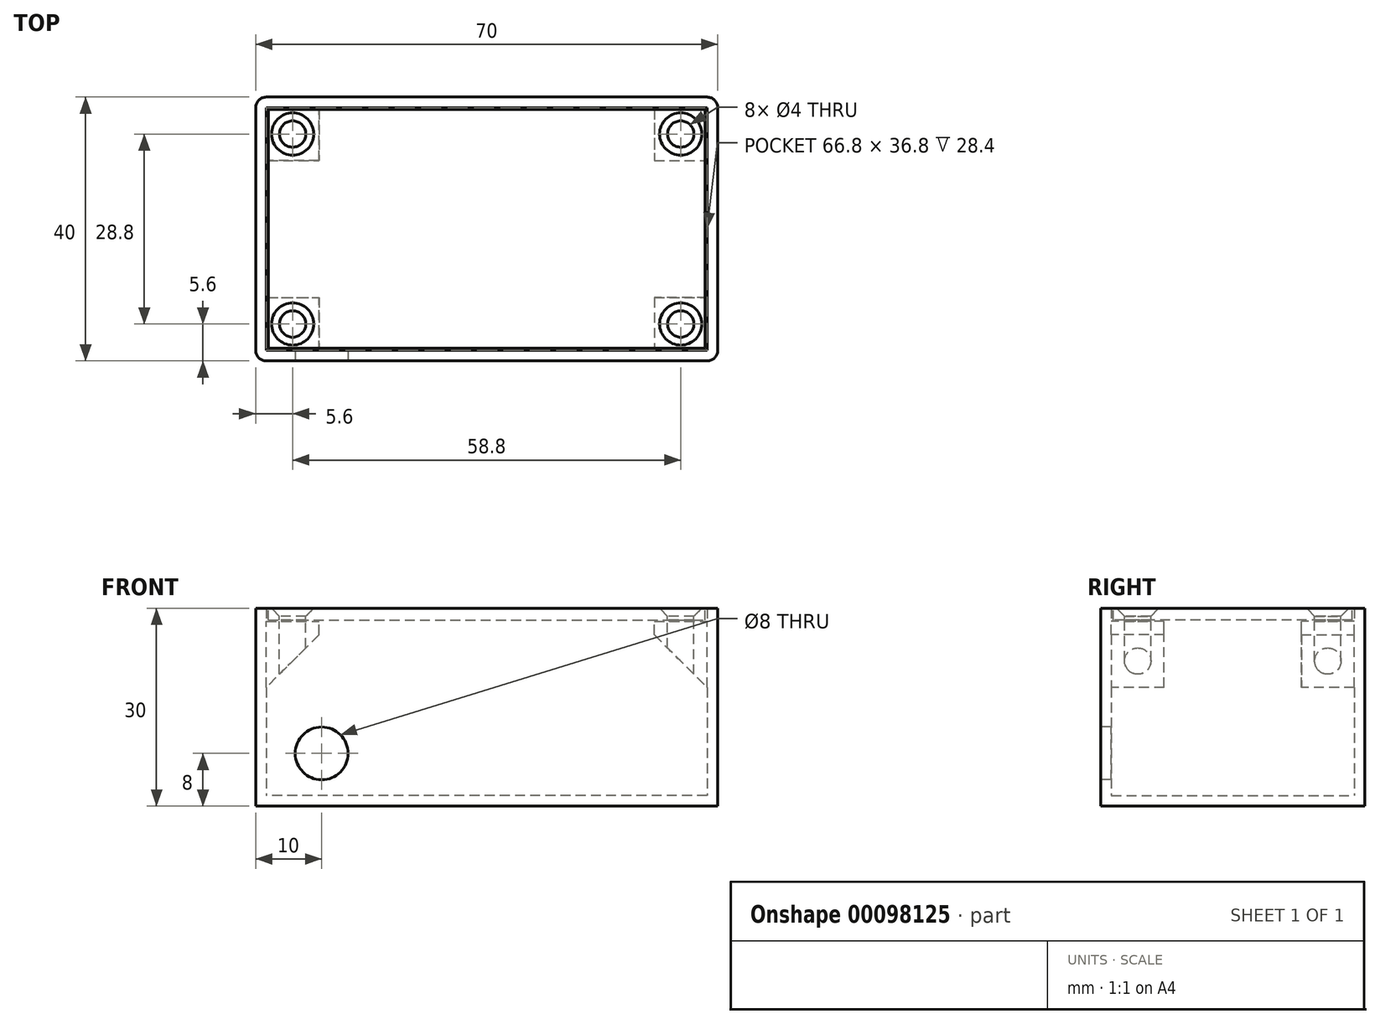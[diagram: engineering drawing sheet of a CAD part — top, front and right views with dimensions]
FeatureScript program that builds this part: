
annotation { "Feature Type Name" : "Feature", "Feature Type Description" : "" }
export const myFeature = defineFeature(function(context is Context, id is Id, definition is map)
    precondition{}
    {
        {
            var Q0;
            Q0=qCreatedBy(makeId("Top.planeOp"),FACE);
            var sketch = newSketch(context, id + "F0", { "sketchPlane" : qUnion([Q0])});
            skLineSegment(sketch, "E0.bottom", {"start": v(0, 0) * mm, "end": v(-70, 0) * mm});
            skLineSegment(sketch, "E0.top", {"start": v(0, 40) * mm, "end": v(-70, 40) * mm});
            skLineSegment(sketch, "E0.left", {"start": v(0, 0) * mm, "end": v(0, 40) * mm});
            skLineSegment(sketch, "E0.right", {"start": v(-70, 0) * mm, "end": v(-70, 40) * mm});
            skSolve(sketch);
        }
        {
            var Q0;
            Q0=makeQuery(id+"F0.imprint","IMPRINT",FACE,{"disambiguationData":[TD([[makeQuery(id+"F0.imprint","IMPRINT",EDGE,{"derivedFrom":sQuery(id+"F0.wireOp",EDGE,"E0.bottom")}),-1.0]])]});
            extrude(context, id + "F1", {"entities" : qUnion([Q0]), "depth" : 30 * mm});
        }
        {
            var Q0;
            Q0=makeQuery(id+"F1.opExtrude","CAP_FACE",FACE,{"disambiguationData":[OSD([sQuery(id+"F0.wireOp",EDGE,"E0.bottom"),sQuery(id+"F0.wireOp",EDGE,"E0.top"),sQuery(id+"F0.wireOp",EDGE,"E0.left"),sQuery(id+"F0.wireOp",EDGE,"E0.right")])],"isStart":false});
            shell(context, id + "F2", {"entities" : qUnion([Q0]), "thickness" : 1.6 * mm});
        }
        {
            var Q0;
            Q0=makeQuery(id+"F1.opExtrude","CAP_FACE",FACE,{"disambiguationData":[OSD([sQuery(id+"F0.wireOp",EDGE,"E0.bottom"),sQuery(id+"F0.wireOp",EDGE,"E0.top"),sQuery(id+"F0.wireOp",EDGE,"E0.left"),sQuery(id+"F0.wireOp",EDGE,"E0.right")])],"isStart":false});
            var Q1;
            Q1 = qBodyType(qCreatedBy(id + "F4" ,EDGE), BodyType.WIRE);
            cPlane(context, id + "F3", {"entities" : qUnion([Q0, Q1]), "cplaneType" : CPlaneType.OFFSET, "offset" : 2 * mm, "oppositeDirection" : true, "width" : 150 * mm, "height" : 150 * mm});
        }
        {
            var Q0;
            Q0=qCreatedBy(id+"F3.planeOp",FACE);
            var sketch = newSketch(context, id + "F4", { "sketchPlane" : qUnion([Q0])});
            skLineSegment(sketch, "E1.bottom", {"start": v(-68.4, 38.4) * mm, "end": v(-60.4, 38.4) * mm});
            skLineSegment(sketch, "E1.top", {"start": v(-68.4, 30.4) * mm, "end": v(-60.4, 30.4) * mm});
            skLineSegment(sketch, "E1.left", {"start": v(-68.4, 38.4) * mm, "end": v(-68.4, 30.4) * mm});
            skLineSegment(sketch, "E1.right", {"start": v(-60.4, 38.4) * mm, "end": v(-60.4, 30.4) * mm});
            skLineSegment(sketch, "E2.bottom", {"start": v(-9.6, 38.4) * mm, "end": v(-1.6, 38.4) * mm});
            skLineSegment(sketch, "E2.top", {"start": v(-9.6, 30.4) * mm, "end": v(-1.6, 30.4) * mm});
            skLineSegment(sketch, "E2.left", {"start": v(-9.6, 38.4) * mm, "end": v(-9.6, 30.4) * mm});
            skLineSegment(sketch, "E2.right", {"start": v(-1.6, 38.4) * mm, "end": v(-1.6, 30.4) * mm});
            skLineSegment(sketch, "E3.bottom", {"start": v(-9.6, 9.6) * mm, "end": v(-1.6, 9.6) * mm});
            skLineSegment(sketch, "E3.top", {"start": v(-9.6, 1.6) * mm, "end": v(-1.6, 1.6) * mm});
            skLineSegment(sketch, "E3.left", {"start": v(-9.6, 9.6) * mm, "end": v(-9.6, 1.6) * mm});
            skLineSegment(sketch, "E3.right", {"start": v(-1.6, 9.6) * mm, "end": v(-1.6, 1.6) * mm});
            skLineSegment(sketch, "E4.bottom", {"start": v(-68.4, 9.6) * mm, "end": v(-60.4, 9.6) * mm});
            skLineSegment(sketch, "E4.top", {"start": v(-68.4, 1.6) * mm, "end": v(-60.4, 1.6) * mm});
            skLineSegment(sketch, "E4.left", {"start": v(-68.4, 9.6) * mm, "end": v(-68.4, 1.6) * mm});
            skLineSegment(sketch, "E4.right", {"start": v(-60.4, 9.6) * mm, "end": v(-60.4, 1.6) * mm});
            skCircle(sketch, "E5", {"center": v(-64.4, 34.4) * mm, "radius": 2 * mm});
            skPoint(sketch, "E5.centerSnap0", {"position": v(-64.4, 38.4) * mm});
            skPoint(sketch, "E5.centerSnap1", {"position": v(-60.4, 34.4) * mm});
            skCircle(sketch, "E6", {"center": v(-5.6, 34.4) * mm, "radius": 2 * mm});
            skPoint(sketch, "E6.centerSnap0", {"position": v(-9.6, 34.4) * mm});
            skPoint(sketch, "E6.centerSnap1", {"position": v(-5.6, 38.4) * mm});
            skCircle(sketch, "E7", {"center": v(-64.4, 5.6) * mm, "radius": 2 * mm});
            skPoint(sketch, "E7.centerSnap0", {"position": v(-60.4, 5.6) * mm});
            skPoint(sketch, "E7.centerSnap1", {"position": v(-64.4, 9.6) * mm});
            skCircle(sketch, "E8", {"center": v(-5.6, 5.6) * mm, "radius": 2 * mm});
            skPoint(sketch, "E8.centerSnap0", {"position": v(-9.6, 5.6) * mm});
            skPoint(sketch, "E8.centerSnap1", {"position": v(-5.6, 9.6) * mm});
            skSolve(sketch);
        }
        {
            var Q0;
            Q0 = qSketchRegion(id + "F4", true);
            extrude(context, id + "F5", {"entities" : qUnion([Q0]), "operationType" : NewBodyOperationType.ADD, "oppositeDirection" : true, "depth" : 10 * mm});
        }
        {
            var Q0;
            Q0=makeQuery(id+"F5.opExtrude","CAP_EDGE",EDGE,{"disambiguationData":[OSD([sQuery(id+"F4.wireOp",EDGE,"E1.right")])],"isStart":false});
            var Q1;
            Q1=makeQuery(id+"F5.opExtrude","CAP_EDGE",EDGE,{"disambiguationData":[OSD([sQuery(id+"F4.wireOp",EDGE,"E2.left")])],"isStart":false});
            var Q2;
            Q2=makeQuery(id+"F5.opExtrude","CAP_EDGE",EDGE,{"disambiguationData":[OSD([sQuery(id+"F4.wireOp",EDGE,"E4.right")])],"isStart":false});
            var Q3;
            Q3=makeQuery(id+"F5.opExtrude","CAP_EDGE",EDGE,{"disambiguationData":[OSD([sQuery(id+"F4.wireOp",EDGE,"E3.left")])],"isStart":false});
            chamfer(context, id + "F6", {"entities" : qUnion([Q0, Q1, Q2, Q3]), "width" : 8 * mm, "tangentPropagation" : true});
        }
        {
            var Q0;
            Q0=makeQuery(id+"F1.opExtrude","SWEPT_FACE",FACE,{"disambiguationData":[OSD([sQuery(id+"F0.wireOp",EDGE,"E0.bottom")])]});
            var sketch = newSketch(context, id + "F7", { "sketchPlane" : qUnion([Q0])});
            skCircle(sketch, "E9", {"center": v(-60, 8) * mm, "radius": 4 * mm});
            skSolve(sketch);
        }
        {
            var Q0;
            Q0 = qSketchRegion(id + "F7", true);
            var Q1;
            Q1=makeQuery(id+"F2.opShell","OFFSET_FACE",FACE,{"disambiguationData":[OSD([sQuery(id+"F0.wireOp",EDGE,"E0.bottom")])]});
            extrude(context, id + "F8", {"entities" : qUnion([Q0]), "operationType" : NewBodyOperationType.REMOVE, "endBound" : BoundingType.UP_TO_SURFACE, "oppositeDirection" : true, "endBoundEntityFace" : qUnion([Q1]), "depth" : 25 * mm});
        }
        {
            var Q0;
            Q0=makeQuery(id+"F1.opExtrude","CAP_FACE",FACE,{"disambiguationData":[OSD([sQuery(id+"F0.wireOp",EDGE,"E0.bottom"),sQuery(id+"F0.wireOp",EDGE,"E0.top"),sQuery(id+"F0.wireOp",EDGE,"E0.left"),sQuery(id+"F0.wireOp",EDGE,"E0.right")])],"isStart":false});
            var sketch = newSketch(context, id + "F9", { "sketchPlane" : qUnion([Q0])});
            skLineSegment(sketch, "E10.bottom", {"start": v(-68.1, 38.1) * mm, "end": v(-1.9, 38.1) * mm});
            skLineSegment(sketch, "E10.top", {"start": v(-68.1, 1.9) * mm, "end": v(-1.9, 1.9) * mm});
            skLineSegment(sketch, "E10.left", {"start": v(-68.1, 38.1) * mm, "end": v(-68.1, 1.9) * mm});
            skLineSegment(sketch, "E10.right", {"start": v(-1.9, 38.1) * mm, "end": v(-1.9, 1.9) * mm});
            skCircle(sketch, "E11", {"center": v(-64.4, 34.4) * mm, "radius": 2 * mm});
            skCircle(sketch, "E12", {"center": v(-5.6, 34.4) * mm, "radius": 2 * mm});
            skCircle(sketch, "E13", {"center": v(-64.4, 5.6) * mm, "radius": 2 * mm});
            skCircle(sketch, "E14", {"center": v(-5.6, 5.6) * mm, "radius": 2 * mm});
            skSolve(sketch);
        }
        {
            var Q0;
            Q0 = qSketchRegion(id + "F9", true);
            extrude(context, id + "F10", {"entities" : qUnion([Q0]), "oppositeDirection" : true, "depth" : 1.8 * mm});
        }
        {
            var Q0;
            Q0=makeQuery(id+"F10.opExtrude","CAP_EDGE",EDGE,{"disambiguationData":[OSD([sQuery(id+"F9.wireOp",EDGE,"E11")])],"isStart":true});
            var Q1;
            Q1=makeQuery(id+"F10.opExtrude","CAP_EDGE",EDGE,{"disambiguationData":[OSD([sQuery(id+"F9.wireOp",EDGE,"E12")])],"isStart":true});
            var Q2;
            Q2=makeQuery(id+"F10.opExtrude","CAP_EDGE",EDGE,{"disambiguationData":[OSD([sQuery(id+"F9.wireOp",EDGE,"E14")])],"isStart":true});
            var Q3;
            Q3=makeQuery(id+"F10.opExtrude","CAP_EDGE",EDGE,{"disambiguationData":[OSD([sQuery(id+"F9.wireOp",EDGE,"E13")])],"isStart":true});
            chamfer(context, id + "F11", {"entities" : qUnion([Q0, Q1, Q2, Q3]), "width" : 1.2 * mm, "tangentPropagation" : true});
        }
        {
            var Q0;
            Q0=makeQuery(id+"F1.opExtrude","SWEPT_EDGE",EDGE,{"disambiguationData":[OSD([sQuery(id+"F0.wireOp",EDGE,"E0.bottom"),sQuery(id+"F0.wireOp",EDGE,"E0.right")])]});
            var Q1;
            Q1=makeQuery(id+"F1.opExtrude","SWEPT_EDGE",EDGE,{"disambiguationData":[OSD([sQuery(id+"F0.wireOp",EDGE,"E0.bottom"),sQuery(id+"F0.wireOp",EDGE,"E0.left")])]});
            var Q2;
            Q2=makeQuery(id+"F1.opExtrude","SWEPT_EDGE",EDGE,{"disambiguationData":[OSD([sQuery(id+"F0.wireOp",EDGE,"E0.top"),sQuery(id+"F0.wireOp",EDGE,"E0.left")])]});
            var Q3;
            Q3=makeQuery(id+"F1.opExtrude","SWEPT_EDGE",EDGE,{"disambiguationData":[OSD([sQuery(id+"F0.wireOp",EDGE,"E0.top"),sQuery(id+"F0.wireOp",EDGE,"E0.right")])]});
            fillet(context, id + "F12", {"entities" : qUnion([Q0, Q1, Q2, Q3]), "radius" : 1.6 * mm, "tangentPropagation" : true, "allowEdgeOverflow" : false});
        }
    });
